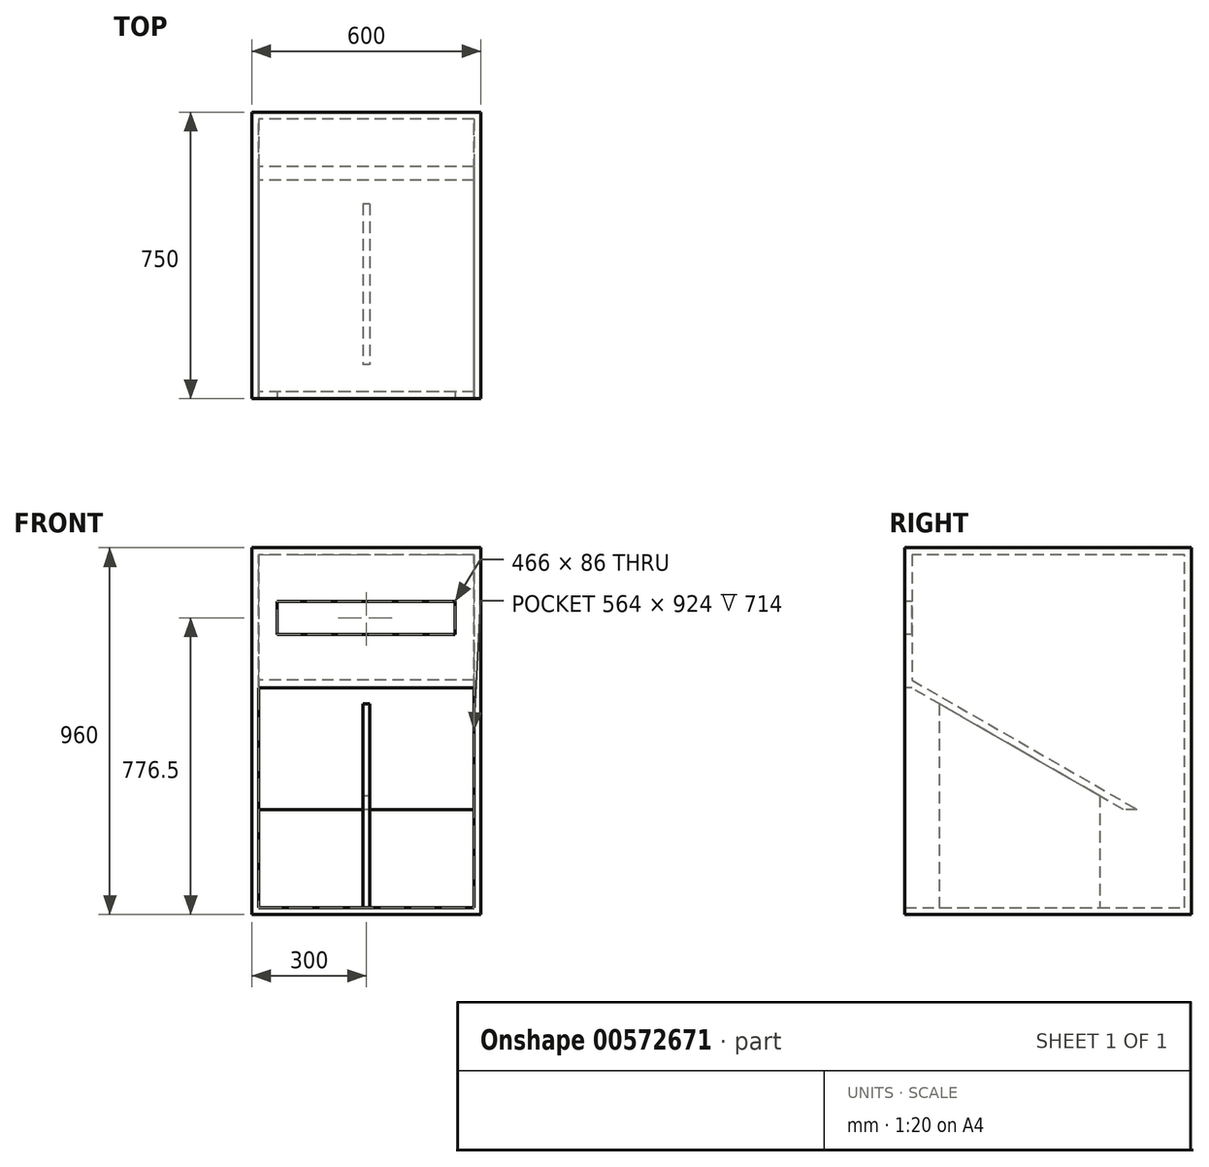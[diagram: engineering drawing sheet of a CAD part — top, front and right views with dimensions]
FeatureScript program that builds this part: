
annotation { "Feature Type Name" : "Feature", "Feature Type Description" : "" }
export const myFeature = defineFeature(function(context is Context, id is Id, definition is map)
    precondition{}
    {
        {
            var Q0;
            Q0=qCreatedBy(makeId("Right.planeOp"),FACE);
            var sketch = newSketch(context, id + "F0", { "sketchPlane" : qUnion([Q0])});
            skLineSegment(sketch, "E0.bottom", {"start": v(0, 0) * mm, "end": v(750, 0) * mm});
            skLineSegment(sketch, "E0.top", {"start": v(0, 960) * mm, "end": v(750, 960) * mm});
            skLineSegment(sketch, "E0.left", {"start": v(0, 0) * mm, "end": v(0, 960) * mm});
            skLineSegment(sketch, "E0.right", {"start": v(750, 0) * mm, "end": v(750, 960) * mm});
            skSolve(sketch);
        }
        {
            var Q0;
            Q0 = qSketchRegion(id + "F0", true);
            extrude(context, id + "F1", {"entities" : qUnion([Q0]), "depth" : 18 * mm, "offsetDistance" : 25 * mm});
        }
        {
            var Q0;
            Q0=makeQuery(id+"F1.opExtrude","CAP_FACE",FACE,{"disambiguationData":[OSD([sQuery(id+"F0.wireOp",EDGE,"E0.bottom"),sQuery(id+"F0.wireOp",EDGE,"E0.top"),sQuery(id+"F0.wireOp",EDGE,"E0.left"),sQuery(id+"F0.wireOp",EDGE,"E0.right")])],"isStart":false});
            var sketch = newSketch(context, id + "F2", { "sketchPlane" : qUnion([Q0])});
            skLineSegment(sketch, "E1", {"start": v(0, 0) * mm, "end": v(0, 18) * mm});
            skLineSegment(sketch, "E2", {"start": v(0, 18) * mm, "end": v(732, 18) * mm});
            skLineSegment(sketch, "E3", {"start": v(732, 18) * mm, "end": v(732, 942) * mm});
            skLineSegment(sketch, "E4", {"start": v(732, 942) * mm, "end": v(18, 942) * mm});
            skLineSegment(sketch, "E5", {"start": v(18, 942) * mm, "end": v(18, 593) * mm});
            skLineSegment(sketch, "E6", {"start": v(18, 593) * mm, "end": v(0, 593) * mm});
            skLineSegment(sketch, "E7", {"start": v(0, 593) * mm, "end": v(0, 960) * mm});
            skLineSegment(sketch, "E8", {"start": v(0, 960) * mm, "end": v(750, 960) * mm});
            skLineSegment(sketch, "E9", {"start": v(750, 960) * mm, "end": v(750, 0) * mm});
            skLineSegment(sketch, "E10", {"start": v(750, 0) * mm, "end": v(0, 0) * mm});
            skLineSegment(sketch, "E11", {"start": v(732, 18) * mm, "end": v(732, 275) * mm});
            skLineSegment(sketch, "E12", {"start": v(732, 275) * mm, "end": v(590, 275) * mm});
            skLineSegment(sketch, "E13", {"start": v(590, 275) * mm, "end": v(572, 275) * mm});
            skLineSegment(sketch, "E14", {"start": v(572, 275) * mm, "end": v(18, 593) * mm});
            skLineSegment(sketch, "E15", {"start": v(18, 593) * mm, "end": v(18, 613.75) * mm});
            skLineSegment(sketch, "E16", {"start": v(18, 613.75) * mm, "end": v(608.15, 275) * mm});
            skLineSegment(sketch, "E17", {"start": v(732, 18) * mm, "end": v(636, 18) * mm});
            skLineSegment(sketch, "E18", {"start": v(732, 18) * mm, "end": v(732, 182) * mm});
            skLineSegment(sketch, "E19", {"start": v(732, 182) * mm, "end": v(636, 18) * mm});
            skSolve(sketch);
        }
        {
            var Q0;
            Q0=makeQuery(id+"F2.imprint","IMPRINT",FACE,{"disambiguationData":[TD([[makeQuery(id+"F2.imprint","IMPRINT",EDGE,{"derivedFrom":sQuery(id+"F2.wireOp",EDGE,"E1")}),-1.0]])]});
            var Q1;
            {var subQ0=sQuery(id+"F2.wireOp",EDGE,"E13");Q1=makeQuery(id+"F2.imprint","IMPRINT",FACE,{"disambiguationData":[TD([[makeQuery(id+"F2.imprint","IMPRINT",EDGE,{"derivedFrom":subQ0}),-1.0]])]});}
            var Q2;
            Q2=makeQuery(id+"F2.imprint","IMPRINT",FACE,{"disambiguationData":[TD([[makeQuery(id+"F2.imprint","IMPRINT",EDGE,{"derivedFrom":sQuery(id+"F2.wireOp",EDGE,"E17")}),-1.0]])]});
            extrude(context, id + "F3", {"entities" : qUnion([Q0, Q1, Q2]), "operationType" : NewBodyOperationType.ADD, "depth" : 564 * mm, "offsetDistance" : 25 * mm});
        }
        {
            var Q0;
            Q0=makeQuery(id+"F3.opExtrude","CAP_FACE",FACE,{"disambiguationData":[OSD([sQuery(id+"F2.wireOp",EDGE,"E1"),sQuery(id+"F2.wireOp",EDGE,"E2"),sQuery(id+"F2.wireOp",EDGE,"E3"),sQuery(id+"F2.wireOp",EDGE,"E4"),sQuery(id+"F2.wireOp",EDGE,"E5"),sQuery(id+"F2.wireOp",EDGE,"E6"),sQuery(id+"F2.wireOp",EDGE,"E7"),sQuery(id+"F2.wireOp",EDGE,"E8"),sQuery(id+"F2.wireOp",EDGE,"E9"),sQuery(id+"F2.wireOp",EDGE,"E10"),sQuery(id+"F2.wireOp",EDGE,"E11"),sQuery(id+"F2.wireOp",EDGE,"E12"),sQuery(id+"F2.wireOp",EDGE,"E13"),sQuery(id+"F2.wireOp",EDGE,"E14"),sQuery(id+"F2.wireOp",EDGE,"E16"),sQuery(id+"F2.wireOp",EDGE,"E19")])],"isStart":false});
            var sketch = newSketch(context, id + "F4", { "sketchPlane" : qUnion([Q0])});
            skLineSegment(sketch, "E20.bottom", {"start": v(0, 960) * mm, "end": v(750, 960) * mm});
            skLineSegment(sketch, "E20.top", {"start": v(0, 0) * mm, "end": v(750, 0) * mm});
            skLineSegment(sketch, "E20.left", {"start": v(0, 960) * mm, "end": v(0, 0) * mm});
            skLineSegment(sketch, "E20.right", {"start": v(750, 960) * mm, "end": v(750, 0) * mm});
            skSolve(sketch);
        }
        {
            var Q0;
            {var subQ2=sQuery(id+"F4.wireOp",EDGE,"E20.bottom");Q0=makeQuery(id+"F4.imprint","IMPRINT",FACE,{"disambiguationData":[TD([[makeQuery(id+"F4.imprint","IMPRINT",EDGE,{"derivedFrom":subQ2}),-1.0]])]});}
            var Q1;
            {var subQ0=makeQuery(id+"F3.opExtrude","CAP_EDGE",EDGE,{"disambiguationData":[OSD([sQuery(id+"F2.wireOp",EDGE,"E2")])],"isStart":false});Q1=makeQuery(id+"F4.imprint","IMPRINT",FACE,{"disambiguationData":[TD([[makeQuery(id+"F4.imprint","IMPRINT",EDGE,{"derivedFrom":subQ0}),1.0]])]});}
            extrude(context, id + "F5", {"entities" : qUnion([Q0, Q1]), "operationType" : NewBodyOperationType.ADD, "depth" : 18 * mm, "offsetDistance" : 25 * mm});
        }
        {
            var Q0;
            Q0=makeQuery(id+"F5.boolean.opBoolean","MERGE",FACE,{"derivedFrom":[makeQuery(id+"F3.boolean.opBoolean","MERGE",FACE,{"derivedFrom":[makeQuery(id+"F1.opExtrude","SWEPT_FACE",FACE,{"disambiguationData":[OSD([sQuery(id+"F0.wireOp",EDGE,"E0.left")])]}),makeQuery(id+"F3.opExtrude","SWEPT_FACE",FACE,{"disambiguationData":[OSD([sQuery(id+"F2.wireOp",EDGE,"E1")])]}),makeQuery(id+"F3.opExtrude","SWEPT_FACE",FACE,{"disambiguationData":[OSD([sQuery(id+"F2.wireOp",EDGE,"E7")])]})]}),makeQuery(id+"F5.opExtrude","SWEPT_FACE",FACE,{"disambiguationData":[OSD([sQuery(id+"F4.wireOp",EDGE,"E20.left")])]})]});
            var sketch = newSketch(context, id + "F6", { "sketchPlane" : qUnion([Q0])});
            skLineSegment(sketch, "E21", {"start": v(0, 960) * mm, "end": v(67, 960) * mm});
            skLineSegment(sketch, "E22", {"start": v(67, 960) * mm, "end": v(67, 819.5) * mm});
            skLineSegment(sketch, "E23.bottom", {"start": v(67, 819.5) * mm, "end": v(533, 819.5) * mm});
            skLineSegment(sketch, "E23.top", {"start": v(67, 733.5) * mm, "end": v(533, 733.5) * mm});
            skLineSegment(sketch, "E23.left", {"start": v(67, 819.5) * mm, "end": v(67, 733.5) * mm});
            skLineSegment(sketch, "E23.right", {"start": v(533, 819.5) * mm, "end": v(533, 733.5) * mm});
            skSolve(sketch);
        }
        {
            var Q0;
            Q0 = qSketchRegion(id + "F6", true);
            extrude(context, id + "F7", {"entities" : qUnion([Q0]), "operationType" : NewBodyOperationType.REMOVE, "oppositeDirection" : true, "depth" : 25 * mm, "offsetDistance" : 25 * mm});
        }
        {
            var Q0;
            Q0=makeQuery(id+"F3.opExtrude","SWEPT_FACE",FACE,{"disambiguationData":[OSD([sQuery(id+"F2.wireOp",EDGE,"E2")])]});
            var sketch = newSketch(context, id + "F8", { "sketchPlane" : qUnion([Q0])});
            skLineSegment(sketch, "E24", {"start": v(18, 0) * mm, "end": v(291, 0) * mm});
            skLineSegment(sketch, "E25", {"start": v(291, 0) * mm, "end": v(291, 90) * mm});
            skLineSegment(sketch, "E26.bottom", {"start": v(291, 90) * mm, "end": v(309, 90) * mm});
            skLineSegment(sketch, "E26.top", {"start": v(291, 510) * mm, "end": v(309, 510) * mm});
            skLineSegment(sketch, "E26.left", {"start": v(291, 90) * mm, "end": v(291, 510) * mm});
            skLineSegment(sketch, "E26.right", {"start": v(309, 90) * mm, "end": v(309, 510) * mm});
            skSolve(sketch);
        }
        {
            var Q0;
            Q0=makeQuery(id+"F8.imprint","IMPRINT",FACE,{"disambiguationData":[TD([[makeQuery(id+"F8.imprint","IMPRINT",EDGE,{"derivedFrom":sQuery(id+"F8.wireOp",EDGE,"E26.bottom")}),1.0]])]});
            extrude(context, id + "F9", {"entities" : qUnion([Q0]), "operationType" : NewBodyOperationType.ADD, "endBound" : BoundingType.UP_TO_NEXT, "depth" : 328 * mm, "offsetDistance" : 25 * mm});
        }
    });
